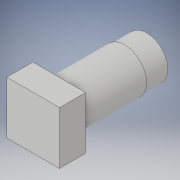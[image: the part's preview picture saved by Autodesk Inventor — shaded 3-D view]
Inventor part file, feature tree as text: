
AUTODESK INVENTOR PART (.ipt)
format: ipt  version: 2018 (Build 220112000, 112)  size: 109,568 bytes
history: native  units: in
note: dims shown in document units (in); Inventor stores cm internally (conversion verified against a paired STEP export)
features: extrude x3, sketch x3
ambient origin geometry x8: Origin, YZ Plane, XZ Plane, XY Plane, X Axis, Y Axis, Z Axis, Center Point
bodies: Solid1 (feature_tree)
feature tree (6):
  extrude  "Extrusion1"  Depth=0.6988in
  extrude  "Extrusion2"  Depth=0.3465in
  extrude  "Extrusion3"  Depth=0.2953in
  sketch  "Sketch1"  dims[d0=0.6988in d1=0.6988in]
  sketch  "Sketch2"  dims[d2=0.3465in d3=0.0in d4=0.5807in]
  sketch  "Sketch3"  dims[d5=0.8661in d6=0.0in d7=0.5556in d8=0.2953in d9=0.0in]
